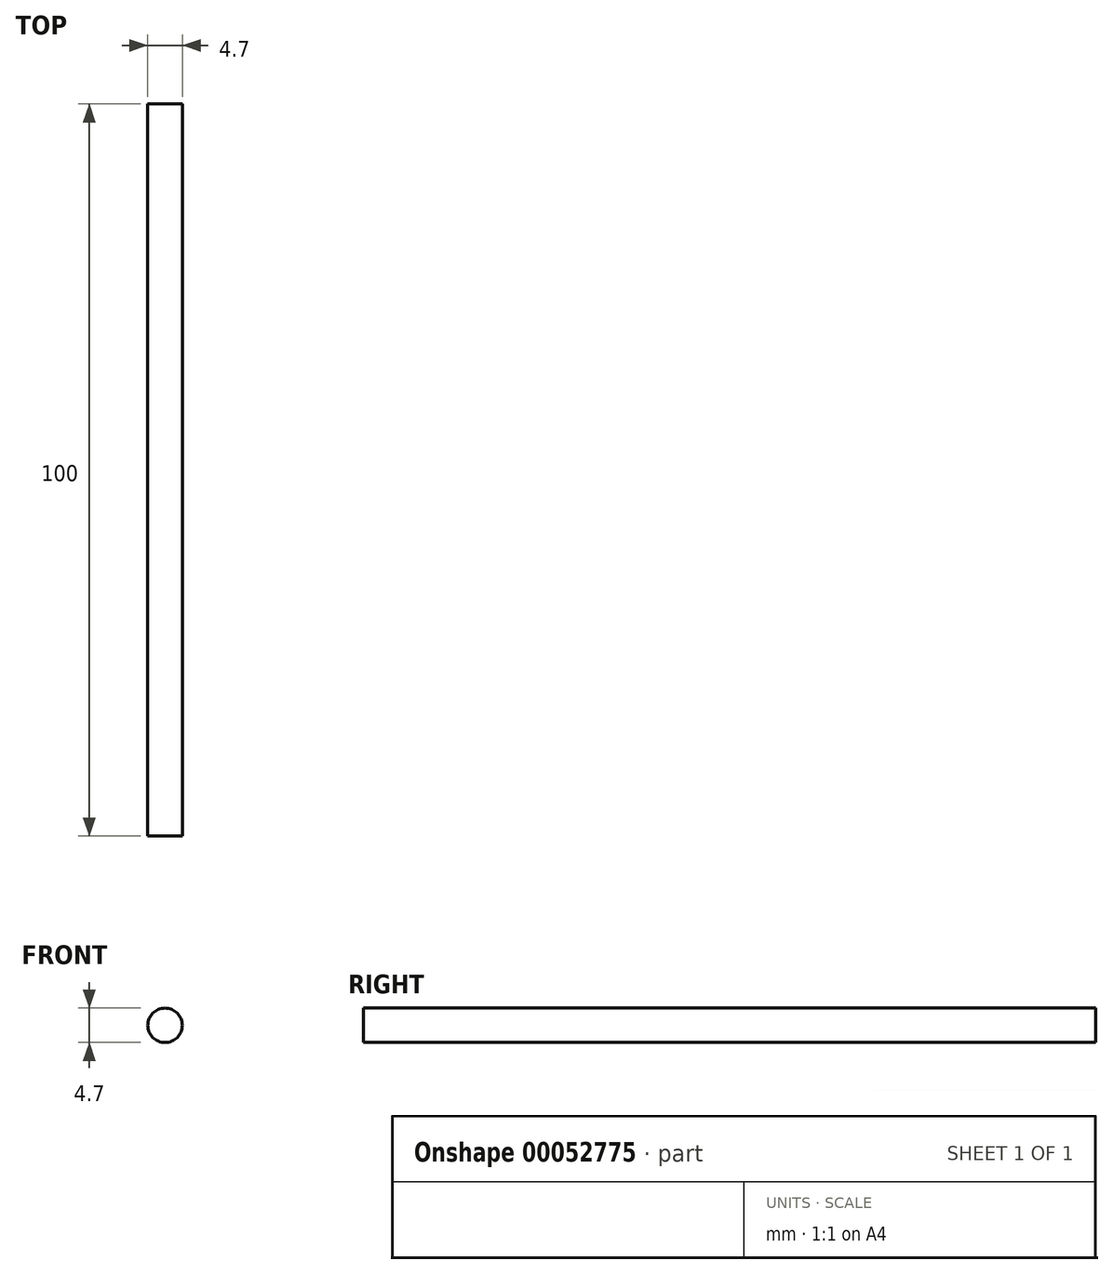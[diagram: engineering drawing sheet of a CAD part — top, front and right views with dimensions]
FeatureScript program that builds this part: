
annotation { "Feature Type Name" : "Feature", "Feature Type Description" : "" }
export const myFeature = defineFeature(function(context is Context, id is Id, definition is map)
    precondition{}
    {
        {
            var Q0;
            Q0=qCreatedBy(makeId("Front.planeOp"),FACE);
            var sketch = newSketch(context, id + "F0", { "sketchPlane" : qUnion([Q0])});
            skCircle(sketch, "E0", {"center": v(0, 0) * mm, "radius": 2.35 * mm});
            skSolve(sketch);
        }
        {
            var Q0;
            Q0=makeQuery(id+"F0.imprint","IMPRINT",FACE,{"disambiguationData":[TD([[makeQuery(id+"F0.imprint","IMPRINT",EDGE,{"derivedFrom":sQuery(id+"F0.wireOp",EDGE,"E0")}),1.0]])]});
            extrude(context, id + "F1", {"entities" : qUnion([Q0]), "oppositeDirection" : true, "depth" : 100 * mm});
        }
    });
